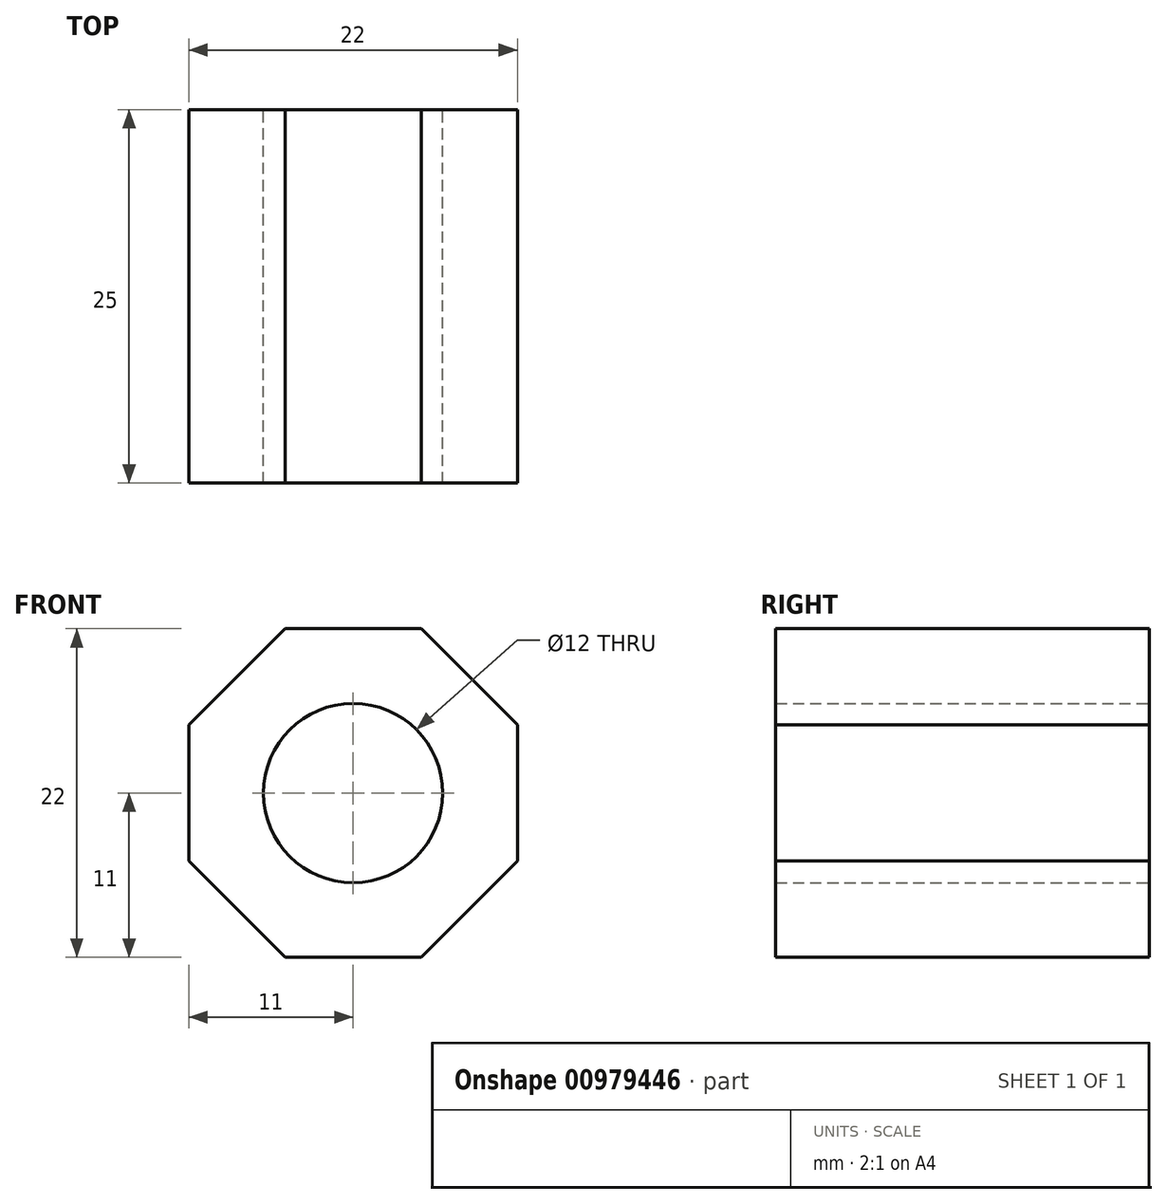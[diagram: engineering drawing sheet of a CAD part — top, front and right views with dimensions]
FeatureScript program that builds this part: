
annotation { "Feature Type Name" : "Feature", "Feature Type Description" : "" }
export const myFeature = defineFeature(function(context is Context, id is Id, definition is map)
    precondition{}
    {
        {
            var Q0;
            Q0=qCreatedBy(makeId("Front.planeOp"),FACE);
            var sketch = newSketch(context, id + "F0", { "sketchPlane" : qUnion([Q0])});
            skCircle(sketch, "E0.cCircle", {"center": v(0, 0) * mm, "radius": 11 * mm, "construction": true});
            skLineSegment(sketch, "E0.0", {"start": v(4.56, 11) * mm, "end": v(11, 4.56) * mm});
            skLineSegment(sketch, "E0.1", {"start": v(11, 4.56) * mm, "end": v(11, -4.56) * mm});
            skLineSegment(sketch, "E0.2", {"start": v(11, -4.56) * mm, "end": v(4.56, -11) * mm});
            skLineSegment(sketch, "E0.3", {"start": v(4.56, -11) * mm, "end": v(-4.56, -11) * mm});
            skLineSegment(sketch, "E0.4", {"start": v(-4.56, -11) * mm, "end": v(-11, -4.56) * mm});
            skLineSegment(sketch, "E0.5", {"start": v(-11, -4.56) * mm, "end": v(-11, 4.56) * mm});
            skLineSegment(sketch, "E0.6", {"start": v(-11, 4.56) * mm, "end": v(-4.56, 11) * mm});
            skLineSegment(sketch, "E0.7", {"start": v(-4.56, 11) * mm, "end": v(4.56, 11) * mm});
            skPoint(sketch, "E0.0.midPoint", {"position": v(7.78, 7.78) * mm});
            skCircle(sketch, "E1", {"center": v(0, 0) * mm, "radius": 6 * mm});
            skSolve(sketch);
        }
        {
            var Q0;
            Q0=makeQuery(id+"F0.imprint","IMPRINT",FACE,{"disambiguationData":[TD([[makeQuery(id+"F0.imprint","IMPRINT",EDGE,{"derivedFrom":sQuery(id+"F0.wireOp",EDGE,"E0.0")}),-1.0]])]});
            extrude(context, id + "F1", {"entities" : qUnion([Q0]), "depth" : 25 * mm, "offsetDistance" : 25.4 * mm});
        }
    });
